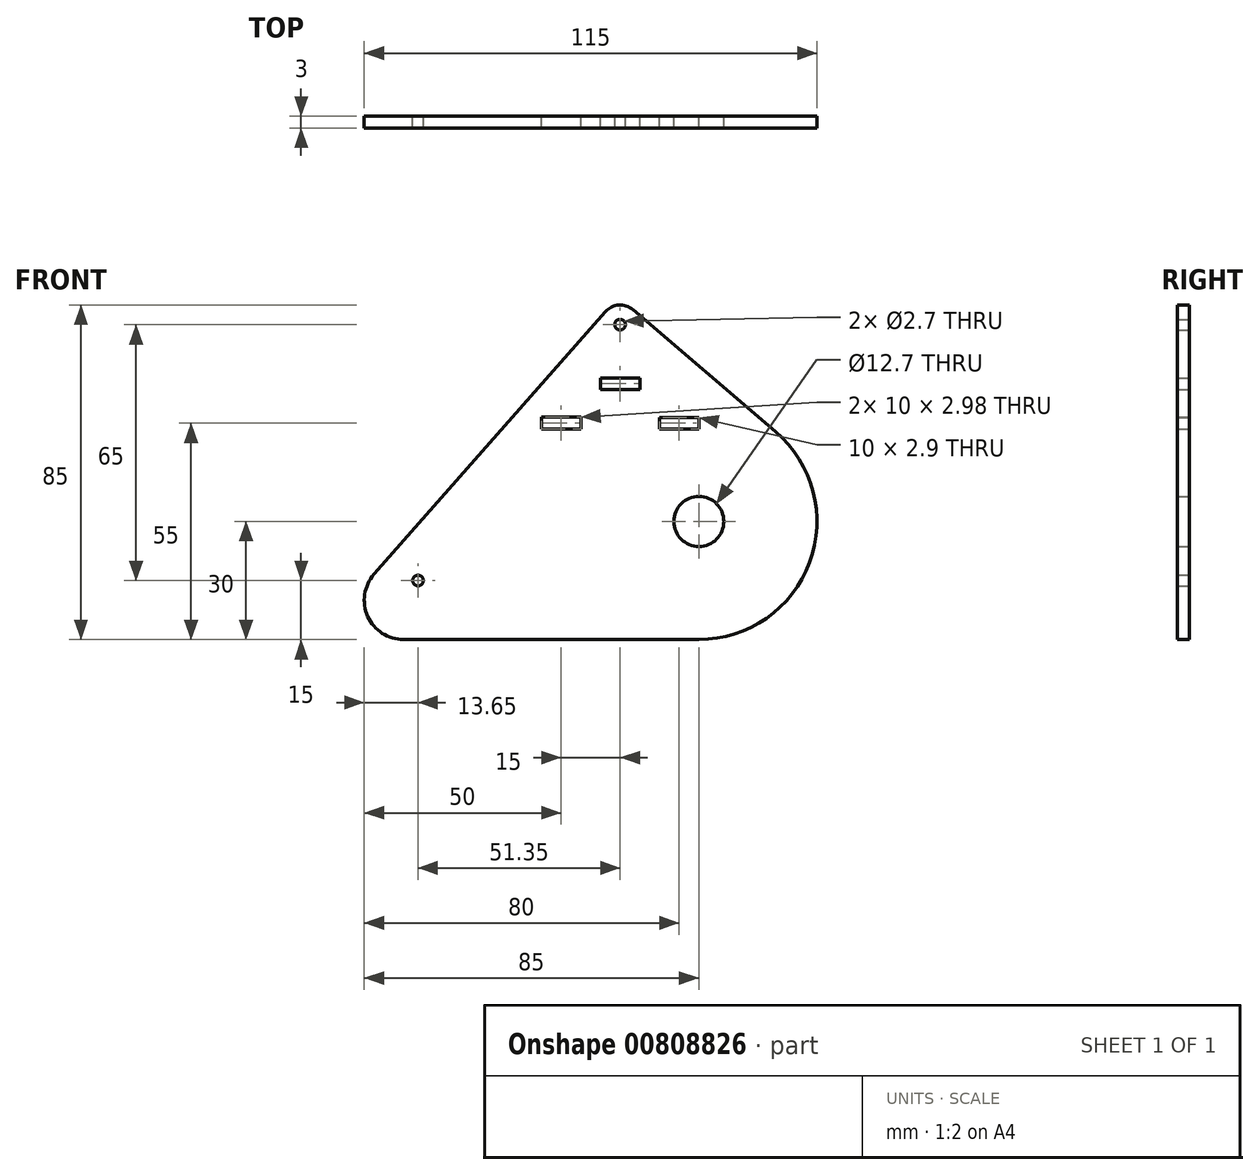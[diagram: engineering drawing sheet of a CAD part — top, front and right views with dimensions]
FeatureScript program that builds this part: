
annotation { "Feature Type Name" : "Feature", "Feature Type Description" : "" }
export const myFeature = defineFeature(function(context is Context, id is Id, definition is map)
    precondition{}
    {
        {
            var Q0;
            Q0=qCreatedBy(makeId("Front.planeOp"),FACE);
            var sketch = newSketch(context, id + "F0", { "sketchPlane" : qUnion([Q0])});
            skLineSegment(sketch, "E0.2", {"start": v(20, -53.51) * mm, "end": v(-55, -53.51) * mm});
            skPoint(sketch, "E0.0.midPoint", {"position": v(-44.64, 24.43) * mm});
            skPoint(sketch, "E1.visualSharp", {"position": v(-89.64, -53.51) * mm});
            skArc(sketch, "E1.filletArc", {"start": v(-70, -20.29) * mm, "mid": v(-73.23, -41.74) * mm, "end": v(-55, -53.51) * mm});
            skLineSegment(sketch, "E2.bottom", {"start": v(50, 6.49) * mm, "end": v(-50, 6.49) * mm});
            skLineSegment(sketch, "E2.top", {"start": v(50, 106.49) * mm, "end": v(-50, 106.5) * mm});
            skLineSegment(sketch, "E2.left", {"start": v(50, 6.49) * mm, "end": v(50, 106.49) * mm});
            skLineSegment(sketch, "E2.right", {"start": v(-50, 6.49) * mm, "end": v(-50, 106.5) * mm});
            skPoint(sketch, "E2.middle", {"position": v(0, 56.49) * mm});
            skPoint(sketch, "E3.visualSharp", {"position": v(100.36, -53.5) * mm});
            skArc(sketch, "E3.filletArc", {"start": v(20, -53.51) * mm, "mid": v(57.52, -27.37) * mm, "end": v(46, 16.89) * mm});
            skPoint(sketch, "E4.visualSharp", {"position": v(0.36, 102.37) * mm});
            skCircle(sketch, "E5", {"center": v(-55, -33.51) * mm, "radius": 1.35 * mm});
            skCircle(sketch, "E6", {"center": v(20, -13.51) * mm, "radius": 1.5 * mm});
            skArc(sketch, "E7", {"start": v(9.75, 47.89) * mm, "mid": v(-1.06, 51.45) * mm, "end": v(-11.26, 46.4) * mm});
            skCircle(sketch, "E8", {"center": v(0, 36.49) * mm, "radius": 1.35 * mm});
            skLineSegment(sketch, "E9", {"start": v(9.75, 47.89) * mm, "end": v(46, 16.89) * mm});
            skPoint(sketch, "E10.orphan", {"position": v(-0.3, 56.49) * mm});
            skLineSegment(sketch, "E11", {"start": v(-70, -20.29) * mm, "end": v(-11.26, 46.4) * mm});
            skArc(sketch, "E12.0", {"start": v(-62.5, -26.9) * mm, "mid": v(-64.11, -37.63) * mm, "end": v(-55, -43.51) * mm});
            skArc(sketch, "E12.1", {"start": v(3.25, 40.29) * mm, "mid": v(-0.35, 41.48) * mm, "end": v(-3.75, 39.8) * mm});
            skLineSegment(sketch, "E12.2", {"start": v(3.25, 40.29) * mm, "end": v(39.5, 9.29) * mm});
            skLineSegment(sketch, "E12.3", {"start": v(-62.5, -26.9) * mm, "end": v(-3.75, 39.8) * mm});
            skArc(sketch, "E12.4", {"start": v(20, -43.5) * mm, "mid": v(48.14, -23.9) * mm, "end": v(39.5, 9.29) * mm});
            skLineSegment(sketch, "E12.5", {"start": v(20, -43.5) * mm, "end": v(-55, -43.5) * mm});
            skLineSegment(sketch, "E13.bottom", {"start": v(10, 10.04) * mm, "end": v(20, 10.04) * mm});
            skLineSegment(sketch, "E13.top", {"start": v(10, 12.94) * mm, "end": v(20, 12.94) * mm});
            skLineSegment(sketch, "E13.left", {"start": v(10, 10.04) * mm, "end": v(10, 12.94) * mm});
            skLineSegment(sketch, "E13.right", {"start": v(20, 10.04) * mm, "end": v(20, 12.94) * mm});
            skPoint(sketch, "E13.middle", {"position": v(15, 11.49) * mm});
            skLineSegment(sketch, "E14.bottom", {"start": v(-20, 10) * mm, "end": v(-10, 10) * mm});
            skLineSegment(sketch, "E14.top", {"start": v(-20, 12.98) * mm, "end": v(-10, 12.98) * mm});
            skLineSegment(sketch, "E14.left", {"start": v(-20, 10) * mm, "end": v(-20, 12.98) * mm});
            skLineSegment(sketch, "E14.right", {"start": v(-10, 10) * mm, "end": v(-10, 12.98) * mm});
            skPoint(sketch, "E14.middle", {"position": v(-15, 11.49) * mm});
            skLineSegment(sketch, "E15.bottom", {"start": v(5, 22.98) * mm, "end": v(-5, 22.98) * mm});
            skLineSegment(sketch, "E15.top", {"start": v(5, 20) * mm, "end": v(-5, 20) * mm});
            skLineSegment(sketch, "E15.left", {"start": v(5, 22.98) * mm, "end": v(5, 20) * mm});
            skLineSegment(sketch, "E15.right", {"start": v(-5, 22.98) * mm, "end": v(-5, 20) * mm});
            skPoint(sketch, "E15.middle", {"position": v(0, 21.49) * mm});
            skCircle(sketch, "E16", {"center": v(-51.35, -28.51) * mm, "radius": 1.35 * mm});
            skCircle(sketch, "E17", {"center": v(20, -13.51) * mm, "radius": 6.35 * mm});
            skSolve(sketch);
        }
        {
            var Q0;
            Q0=makeQuery(id+"F0.imprint","IMPRINT",FACE,{"disambiguationData":[TD([[makeQuery(id+"F0.imprint","IMPRINT",EDGE,{"derivedFrom":sQuery(id+"F0.wireOp",EDGE,"E8")}),-1.0]])]});
            var Q1;
            Q1=makeQuery(id+"F0.imprint","IMPRINT",FACE,{"disambiguationData":[TD([[makeQuery(id+"F0.imprint","IMPRINT",EDGE,{"derivedFrom":sQuery(id+"F0.wireOp",EDGE,"E5")}),-1.0]])]});
            var Q2;
            Q2=makeQuery(id+"F0.imprint","IMPRINT",FACE,{"disambiguationData":[TD([[makeQuery(id+"F0.imprint","IMPRINT",EDGE,{"derivedFrom":sQuery(id+"F0.wireOp",EDGE,"E5")}),1.0]])]});
            extrude(context, id + "F1", {"entities" : qUnion([Q0, Q1, Q2]), "depth" : 3 * mm, "offsetDistance" : 25 * mm});
        }
    });
